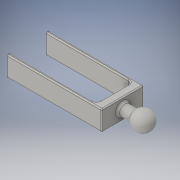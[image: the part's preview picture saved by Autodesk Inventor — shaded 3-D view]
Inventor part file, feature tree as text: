
AUTODESK INVENTOR PART (.ipt)
format: ipt  version: 2016 (Build 200138000, 138)  size: 184,320 bytes
history: native  units: mm
features: fillet x3, sketch x3, extrude x2, projected_geometry x2, other x1, plane x1, revolve x1
ambient origin geometry x8: Origin, YZ Plane, XZ Plane, XY Plane, X Axis, Y Axis, Z Axis, Center Point
bodies: Solid1 (feature_tree)
feature tree (13):
  extrude  "Extrusion1"  Depth=19.8mm
  extrude  "Extrusion2"  Depth=4.0mm
  other  "Work Axis1"
  plane  "Work Plane1"
  revolve  "Revolution1"  [1 undecoded]
  fillet  "Fillet1"  Radius=9.5mm
  fillet  "Fillet2"  Radius=4.5mm
  fillet  "Fillet3"  [1 undecoded]
  sketch  "Sketch1"  dims[d0=17.0mm d1=19.8mm]
  sketch  "Sketch2"  dims[d2=45.0mm d3=4.0mm]
  projected_geometry  "Projected Loop1"
  sketch  "Sketch3"  dims[d4=9.5mm d5=0.0mm d6=5.0mm d7=9.5mm d8=0.0mm d9=4.5mm d10=90.0deg d11=1.0mm d12=2.0mm d13=0.5mm]
  projected_geometry  "Projected Loop2"
note: 2 required parameter values undecoded (feature->parameter linkage not recoverable at this tier; creation-order binding heuristic only, values carry confidence <= 0.55)